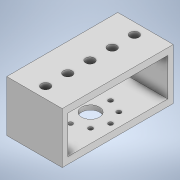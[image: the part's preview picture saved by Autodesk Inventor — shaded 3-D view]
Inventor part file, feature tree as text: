
AUTODESK INVENTOR PART (.ipt)
format: ipt  version: 2021 (Build 250183000, 183)  size: 197,120 bytes
history: native  units: mm
features: extrude x6, sketch x6
ambient origin geometry x8: Origin, YZ Plane, XZ Plane, XY Plane, X Axis, Y Axis, Z Axis, Center Point
bodies: Solide1 (feature_tree)
feature tree (12):
  extrude  "Extrusion1"  Depth=25.0mm
  extrude  "Extrusion2"  Depth=50.0mm
  extrude  "Extrusion4"  Depth=22.0mm
  extrude  "Extrusion5"  Depth=12.75mm
  extrude  "Extrusion6"  Depth=25.0mm
  extrude  "Extrusion7"  Depth=8.0mm
  sketch  "Esquisse1"
  sketch  "Esquisse4"
  sketch  "Esquisse7"
  sketch  "Esquisse8"
  sketch  "Esquisse9"
  sketch  "Esquisse10"
